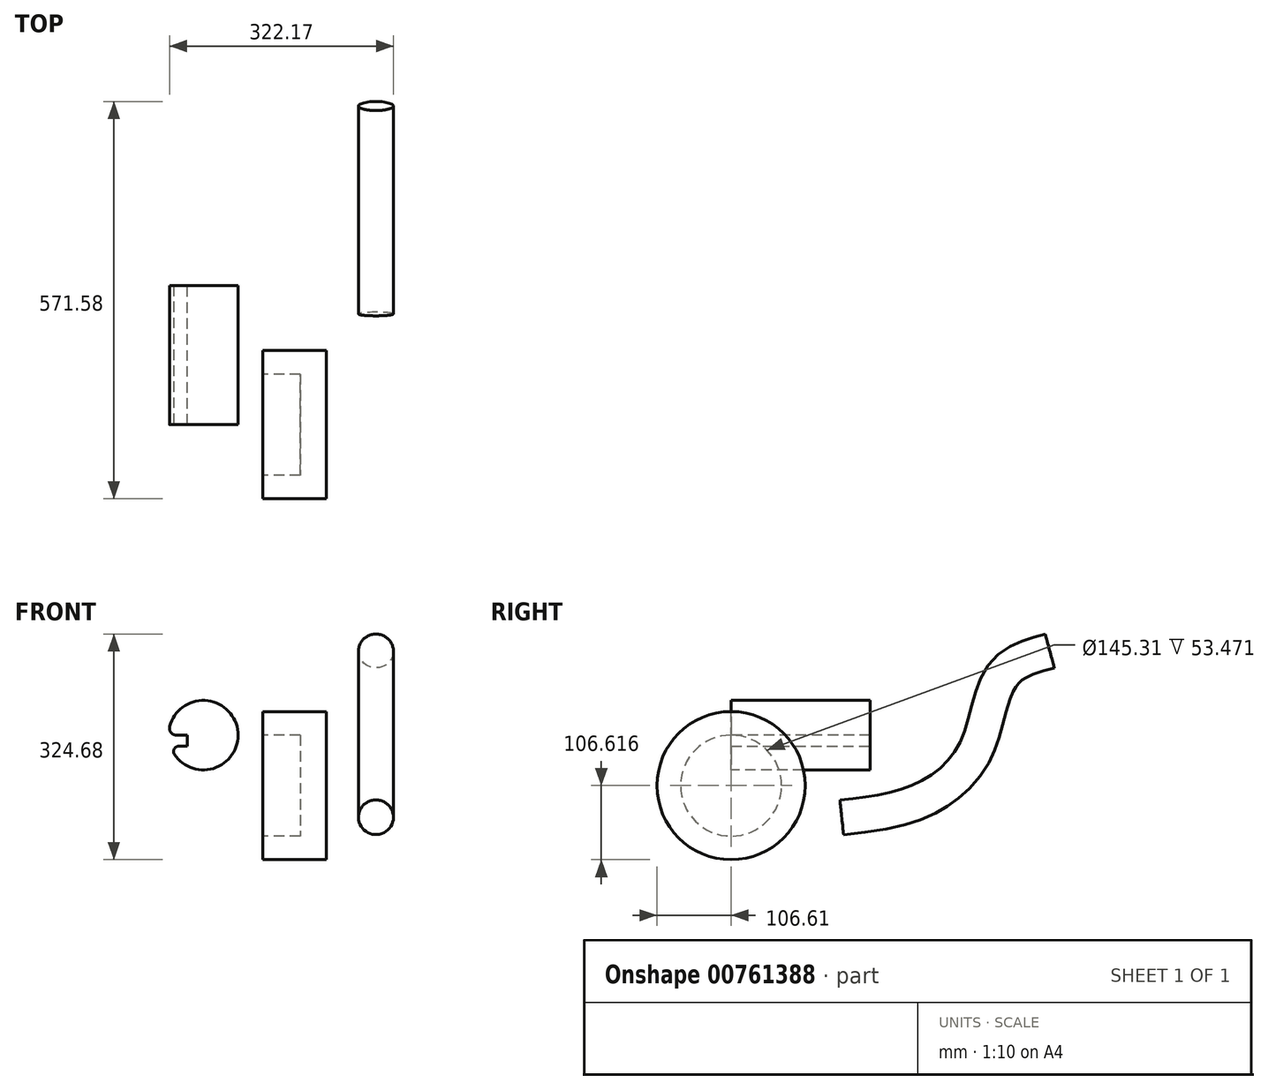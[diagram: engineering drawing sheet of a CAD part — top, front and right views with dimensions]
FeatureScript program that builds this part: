
annotation { "Feature Type Name" : "Feature", "Feature Type Description" : "" }
export const myFeature = defineFeature(function(context is Context, id is Id, definition is map)
    precondition{}
    {
        {
            var Q0;
            Q0=qCreatedBy(makeId("Front.planeOp"),FACE);
            var sketch = newSketch(context, id + "F0", { "sketchPlane" : qUnion([Q0])});
            skCircle(sketch, "E0", {"center": v(0, 0) * mm, "radius": 50 * mm});
            skLineSegment(sketch, "E1.bottom", {"start": v(85.84, 33.96) * mm, "end": v(177.1, 33.96) * mm});
            skLineSegment(sketch, "E1.top", {"start": v(85.84, 0) * mm, "end": v(139.32, 0) * mm});
            skLineSegment(sketch, "E1.left", {"start": v(85.84, 33.96) * mm, "end": v(85.84, 0) * mm});
            skLineSegment(sketch, "E2.top", {"start": v(139.32, -72.65) * mm, "end": v(176.95, -72.65) * mm});
            skLineSegment(sketch, "E2.left", {"start": v(139.32, 0) * mm, "end": v(139.32, -72.65) * mm});
            skLineSegment(sketch, "E3", {"start": v(177.1, 33.96) * mm, "end": v(176.95, -72.65) * mm});
            skSolve(sketch);
        }
        {
            var Q0;
            Q0=makeQuery(id+"F0.imprint","IMPRINT",FACE,{"disambiguationData":[TD([[makeQuery(id+"F0.imprint","IMPRINT",EDGE,{"derivedFrom":sQuery(id+"F0.wireOp",EDGE,"E0")}),1.0]])]});
            extrude(context, id + "F1", {"entities" : qUnion([Q0]), "oppositeDirection" : true, "depth" : 200 * mm, "offsetDistance" : 25 * mm});
        }
        {
            var Q0;
            Q0=makeQuery(id+"F1.opExtrude","CAP_FACE",FACE,{"disambiguationData":[OSD([sQuery(id+"F0.wireOp",EDGE,"E0")])],"isStart":false});
            var sketch = newSketch(context, id + "F2", { "sketchPlane" : qUnion([Q0])});
            skLineSegment(sketch, "E4.bottom", {"start": v(23.37, 0) * mm, "end": v(78.37, 0) * mm});
            skLineSegment(sketch, "E4.top", {"start": v(23.37, -16) * mm, "end": v(78.37, -16) * mm});
            skLineSegment(sketch, "E4.left", {"start": v(23.37, 0) * mm, "end": v(23.37, -16) * mm});
            skLineSegment(sketch, "E4.right", {"start": v(78.37, 0) * mm, "end": v(78.37, -16) * mm});
            skSolve(sketch);
        }
        {
            var Q0;
            Q0 = qSketchRegion(id + "F2", true);
            extrude(context, id + "F3", {"entities" : qUnion([Q0]), "operationType" : NewBodyOperationType.REMOVE, "endBound" : BoundingType.THROUGH_ALL, "oppositeDirection" : true, "depth" : 103 * mm, "offsetDistance" : 25 * mm});
        }
        {
            var Q0;
            Q0=makeQuery(id+"F3.boolean.opBoolean","INTERSECT",EDGE,{"derivedFrom":[makeQuery(id+"F1.opExtrude","SWEPT_FACE",FACE,{"disambiguationData":[OSD([sQuery(id+"F0.wireOp",EDGE,"E0")])]}),makeQuery(id+"F3.opExtrude","SWEPT_FACE",FACE,{"disambiguationData":[OSD([sQuery(id+"F2.wireOp",EDGE,"E4.bottom")])]})]});
            fillet(context, id + "F4", {"entities" : qUnion([Q0]), "radius" : 10 * mm, "tangentPropagation" : true, "allowEdgeOverflow" : false});
        }
        {
            var Q0;
            Q0=makeQuery(id+"F3.boolean.opBoolean","INTERSECT",EDGE,{"derivedFrom":[makeQuery(id+"F1.opExtrude","SWEPT_FACE",FACE,{"disambiguationData":[OSD([sQuery(id+"F0.wireOp",EDGE,"E0")])]}),makeQuery(id+"F3.opExtrude","SWEPT_FACE",FACE,{"disambiguationData":[OSD([sQuery(id+"F2.wireOp",EDGE,"E4.top")])]})]});
            fillet(context, id + "F5", {"entities" : qUnion([Q0]), "radius" : 7.5 * mm, "tangentPropagation" : true, "allowEdgeOverflow" : false});
        }
        {
            var Q0;
            Q0=makeQuery(id+"F0.imprint","IMPRINT",FACE,{"disambiguationData":[TD([[makeQuery(id+"F0.imprint","IMPRINT",EDGE,{"derivedFrom":sQuery(id+"F0.wireOp",EDGE,"E1.bottom")}),-1.0]])]});
            var Q1;
            Q1=sQuery(id+"F0.wireOp",EDGE,"E2.top");
            revolve(context, id + "F6", {"surfaceOperationType" : NewSurfaceOperationType.NEW, "entities" : qUnion([Q0]), "axis" : qUnion([Q1]), "revolveType" : RevolveType.FULL});
        }
        {
            var Q0;
            Q0=makeQuery(id+"F6.opRevolve","SWEPT_FACE",FACE,{"disambiguationData":[OSD([sQuery(id+"F0.wireOp",EDGE,"E2.left")])]});
            cPlane(context, id + "F7", {"entities" : qUnion([Q0]), "cplaneType" : CPlaneType.OFFSET, "offset" : 109 * mm, "oppositeDirection" : true, "width" : 150 * mm, "height" : 150 * mm});
        }
        {
            var Q0;
            Q0=qCreatedBy(id+"F7.planeOp",FACE);
            var sketch = newSketch(context, id + "F8", { "sketchPlane" : qUnion([Q0])});
            skFitSpline(sketch, "E5", {"points": [v(-159.15, -118.16) * mm, v(-269.4, -95.76) * mm, v(-351.85, -21.37) * mm, v(-390.39, 86.18) * mm, v(-458.5, 121.13) * mm], "startDerivative": vector(-434.21, 45.38) * mm, "endDerivative": vector(-366.6, 97.6) * mm});
            skSolve(sketch);
        }
        {
            var Q0;
            Q0=sQuery(id+"F8.wireOp",EDGE,"E5");
            var Q1;
            Q1=sQuery(id+"F8.wireOp",VERTEX,"E5.start");
            cPlane(context, id + "F9", {"entities" : qUnion([Q0, Q1]), "cplaneType" : CPlaneType.CURVE_POINT, "offset" : 25 * mm, "width" : 150 * mm, "height" : 150 * mm});
        }
        {
            var Q0;
            Q0=qCreatedBy(id+"F9.planeOp",FACE);
            var sketch = newSketch(context, id + "F10", { "sketchPlane" : qUnion([Q0])});
            skCircle(sketch, "E6", {"center": v(-248.32, -134.07) * mm, "radius": 25.13 * mm});
            skSolve(sketch);
        }
        {
            var Q0;
            Q0=makeQuery(id+"F10.imprint","IMPRINT",FACE,{"disambiguationData":[TD([[makeQuery(id+"F10.imprint","IMPRINT",EDGE,{"derivedFrom":sQuery(id+"F10.wireOp",EDGE,"E6")}),1.0]])]});
            var Q1;
            Q1=sQuery(id+"F8.wireOp",EDGE,"E5");
            sweep(context, id + "F11", {"profiles" : qUnion([Q0]), "path" : qUnion([Q1])});
        }
    });
